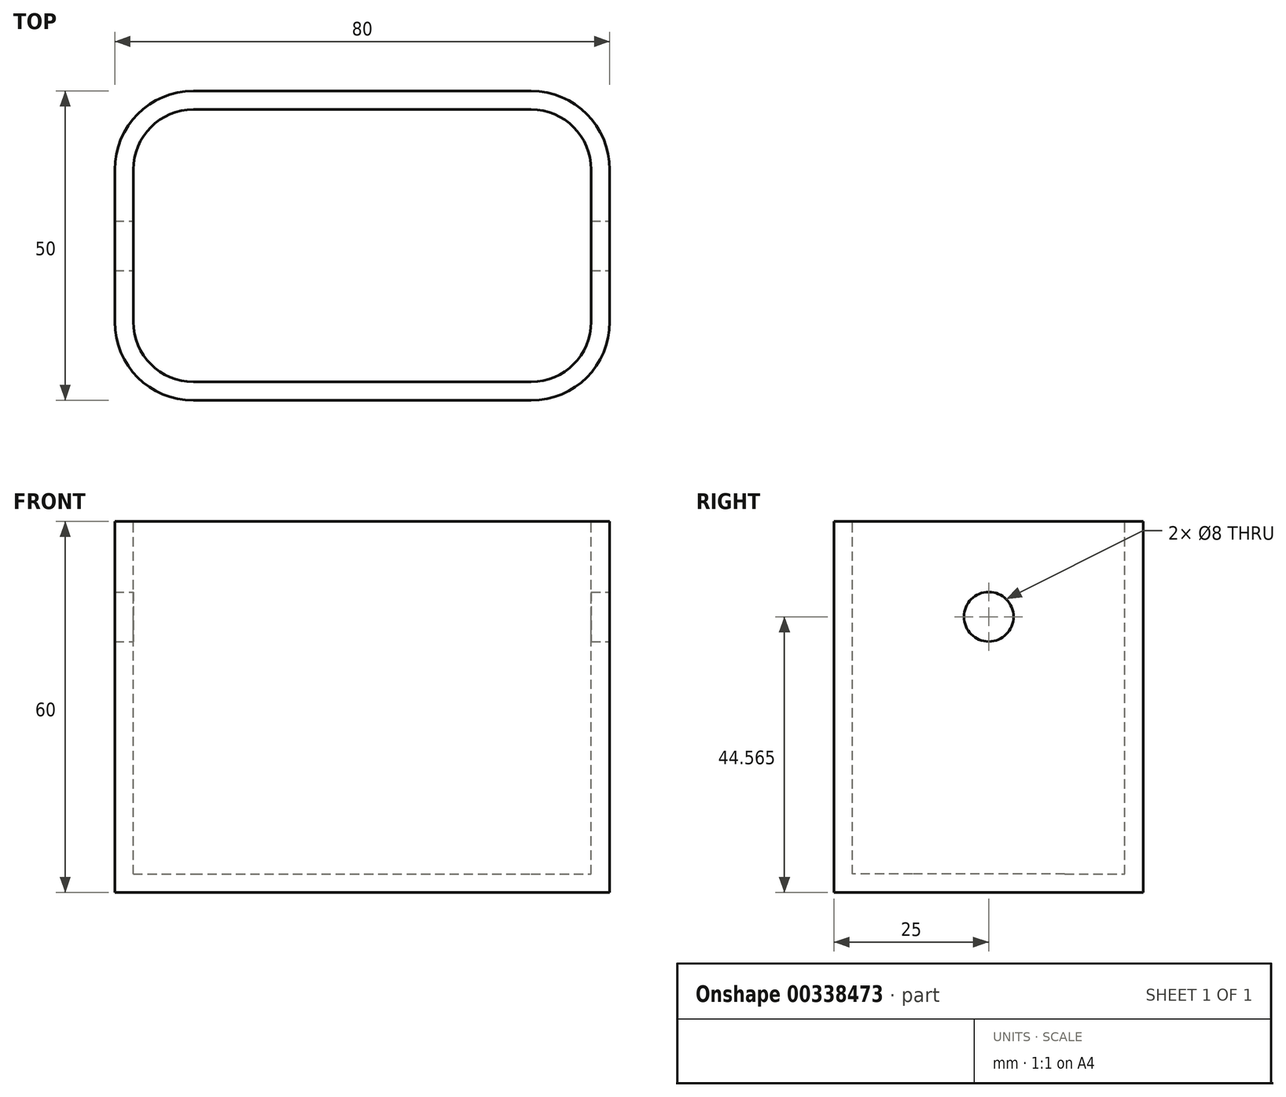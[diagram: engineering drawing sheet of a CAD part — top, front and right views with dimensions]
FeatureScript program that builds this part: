
annotation { "Feature Type Name" : "Feature", "Feature Type Description" : "" }
export const myFeature = defineFeature(function(context is Context, id is Id, definition is map)
    precondition{}
    {
        {
            var Q0;
            Q0=qCreatedBy(makeId("Top.planeOp"),FACE);
            var sketch = newSketch(context, id + "F0", { "sketchPlane" : qUnion([Q0])});
            skLineSegment(sketch, "E0.bottom", {"start": v(-42.13, 25) * mm, "end": v(37.87, 25) * mm});
            skLineSegment(sketch, "E0.top", {"start": v(-42.13, -25) * mm, "end": v(37.87, -25) * mm});
            skLineSegment(sketch, "E0.left", {"start": v(-42.13, 25) * mm, "end": v(-42.13, -25) * mm});
            skLineSegment(sketch, "E0.right", {"start": v(37.87, 25) * mm, "end": v(37.87, -25) * mm});
            skCircle(sketch, "E1", {"center": v(-15.79, 49.85) * mm, "radius": 4.37 * mm});
            skSolve(sketch);
        }
        {
            var Q0;
            Q0=makeQuery(id+"F0.imprint","IMPRINT",FACE,{"disambiguationData":[TD([[makeQuery(id+"F0.imprint","IMPRINT",EDGE,{"derivedFrom":sQuery(id+"F0.wireOp",EDGE,"E0.bottom")}),-1.0]])]});
            extrude(context, id + "F1", {"entities" : qUnion([Q0]), "depth" : 60 * mm});
        }
        {
            var Q0;
            Q0=makeQuery(id+"F1.opExtrude","SWEPT_EDGE",EDGE,{"disambiguationData":[OSD([sQuery(id+"F0.wireOp",EDGE,"E0.top"),sQuery(id+"F0.wireOp",EDGE,"E0.left")])]});
            var Q1;
            Q1=makeQuery(id+"F1.opExtrude","SWEPT_EDGE",EDGE,{"disambiguationData":[OSD([sQuery(id+"F0.wireOp",EDGE,"E0.bottom"),sQuery(id+"F0.wireOp",EDGE,"E0.right")])]});
            var Q2;
            Q2=makeQuery(id+"F1.opExtrude","SWEPT_EDGE",EDGE,{"disambiguationData":[OSD([sQuery(id+"F0.wireOp",EDGE,"E0.top"),sQuery(id+"F0.wireOp",EDGE,"E0.right")])]});
            var Q3;
            Q3=makeQuery(id+"F1.opExtrude","SWEPT_EDGE",EDGE,{"disambiguationData":[OSD([sQuery(id+"F0.wireOp",EDGE,"E0.bottom"),sQuery(id+"F0.wireOp",EDGE,"E0.left")])]});
            fillet(context, id + "F2", {"entities" : qUnion([Q0, Q1, Q2, Q3]), "radius" : 12.7 * mm, "tangentPropagation" : true, "allowEdgeOverflow" : false});
        }
        {
            var Q0;
            Q0=makeQuery(id+"F1.opExtrude","CAP_FACE",FACE,{"disambiguationData":[OSD([sQuery(id+"F1q6g8jRJRVMzjX_0.wireOp",EDGE,"GZDelA3o-2cIQ-npDF-fh1f-AlR4BgICvqZV.bottom"),sQuery(id+"F1q6g8jRJRVMzjX_0.wireOp",EDGE,"GZDelA3o-2cIQ-npDF-fh1f-AlR4BgICvqZV.top"),sQuery(id+"F1q6g8jRJRVMzjX_0.wireOp",EDGE,"GZDelA3o-2cIQ-npDF-fh1f-AlR4BgICvqZV.left"),sQuery(id+"F1q6g8jRJRVMzjX_0.wireOp",EDGE,"GZDelA3o-2cIQ-npDF-fh1f-AlR4BgICvqZV.right")])],"isStart":false});
            var Q1;
            Q1=makeQuery(id+"F1.opExtrude","CAP_FACE",FACE,{"disambiguationData":[OSD([sQuery(id+"F0.wireOp",EDGE,"E0.bottom"),sQuery(id+"F0.wireOp",EDGE,"E0.top"),sQuery(id+"F0.wireOp",EDGE,"E0.left"),sQuery(id+"F0.wireOp",EDGE,"E0.right")])],"isStart":false});
            shell(context, id + "F3", {"entities" : qUnion([Q0, Q1]), "thickness" : 3 * mm});
        }
        {
            var Q0;
            Q0=makeQuery(id+"F1.opExtrude","SWEPT_FACE",FACE,{"disambiguationData":[OSD([sQuery(id+"F0.wireOp",EDGE,"E0.right")])]});
            var sketch = newSketch(context, id + "F4", { "sketchPlane" : qUnion([Q0])});
            skCircle(sketch, "E2", {"center": v(0, 44.56) * mm, "radius": 5.9 * mm});
            skSolve(sketch);
        }
        {
            var Q0;
            Q0=sQuery(id+"F4.wireOp",VERTEX,"E2.center");
            var Q1;
            Q1=makeQuery(id+"F1.opExtrude","SWEPT_BODY",BODY,{"disambiguationData":[OSD([sQuery(id+"F0.wireOp",EDGE,"E0.bottom"),sQuery(id+"F0.wireOp",EDGE,"E0.top"),sQuery(id+"F0.wireOp",EDGE,"E0.left"),sQuery(id+"F0.wireOp",EDGE,"E0.right")])]});
            hole(context, id + "F5", {"style" : HoleStyle.SIMPLE, "endStyle" : HoleEndStyle.THROUGH, "standardTappedOrClearance" : lookupTablePath({ "standard" : "ISO", "size" : "5", "type" : "鑽孔" }), "standardBlindInLast" : lookupTablePath({ "standard" : "ISO", "size" : "5", "type" : "鑽孔" }), "holeDiameter" : 8 * mm, "tappedDepth" : 12.7 * mm, "tapClearance" : 3, "locations" : qUnion([Q0]), "scope" : qUnion([Q1])});
        }
    });
